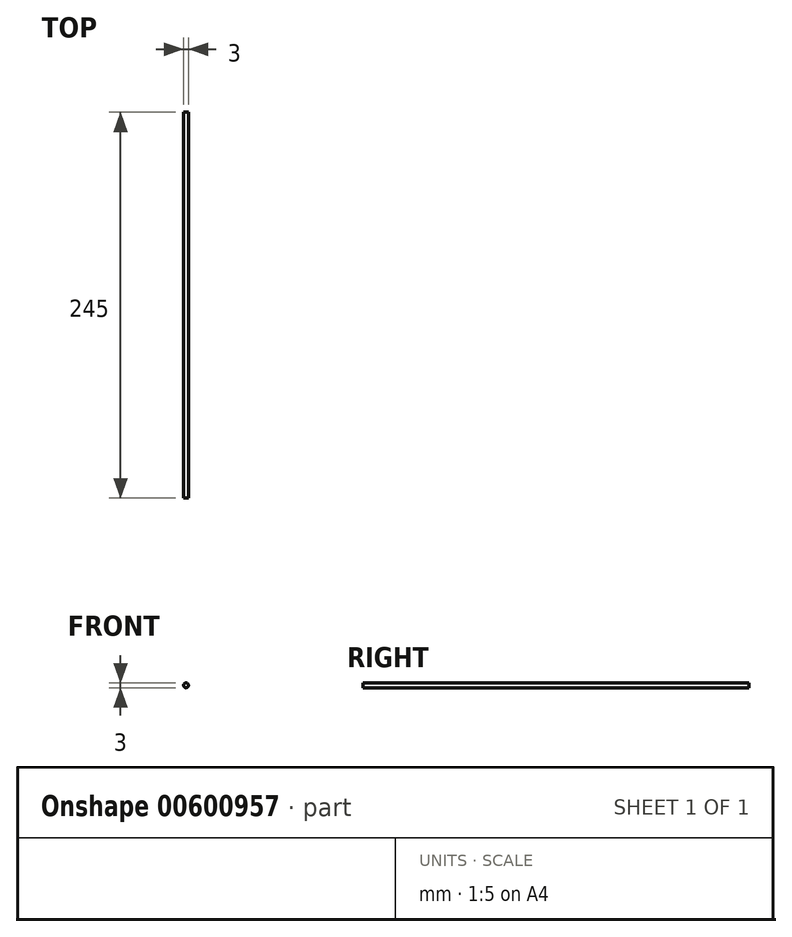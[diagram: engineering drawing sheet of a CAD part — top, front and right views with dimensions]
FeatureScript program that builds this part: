
annotation { "Feature Type Name" : "Feature", "Feature Type Description" : "" }
export const myFeature = defineFeature(function(context is Context, id is Id, definition is map)
    precondition{}
    {
        {
            var Q0;
            Q0=qCreatedBy(makeId("Front.planeOp"),FACE);
            var sketch = newSketch(context, id + "F0", { "sketchPlane" : qUnion([Q0])});
            skCircle(sketch, "E0", {"center": v(0, 0) * mm, "radius": 1.5 * mm});
            skSolve(sketch);
        }
        {
            var Q0;
            Q0=makeQuery(id+"F0.imprint","IMPRINT",FACE,{"disambiguationData":[TD([[makeQuery(id+"F0.imprint","IMPRINT",EDGE,{"derivedFrom":sQuery(id+"F0.wireOp",EDGE,"E0")}),1.0]])]});
            extrude(context, id + "F1", {"entities" : qUnion([Q0]), "depth" : 245 * mm, "offsetDistance" : 25 * mm});
        }
    });
